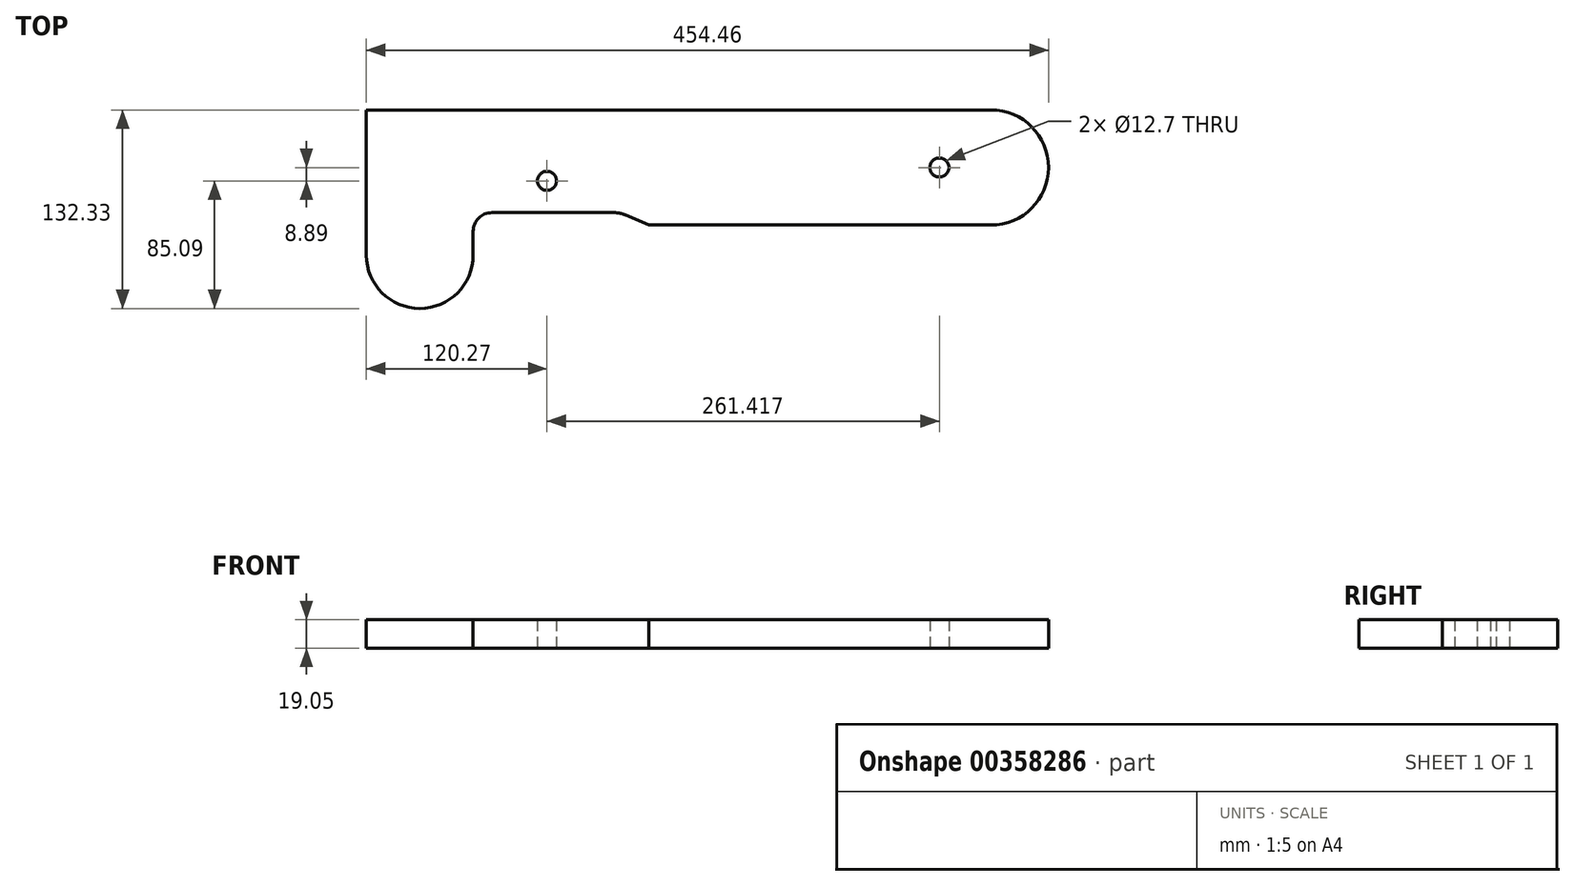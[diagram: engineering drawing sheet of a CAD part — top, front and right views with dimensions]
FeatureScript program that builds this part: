
annotation { "Feature Type Name" : "Feature", "Feature Type Description" : "" }
export const myFeature = defineFeature(function(context is Context, id is Id, definition is map)
    precondition{}
    {
        {
            var Q0;
            Q0=qCreatedBy(makeId("Top.planeOp"),FACE);
            var sketch = newSketch(context, id + "F0", { "sketchPlane" : qUnion([Q0])});
            skCircle(sketch, "E0", {"center": v(0, 0) * mm, "radius": 6.35 * mm});
            skCircle(sketch, "E1", {"center": v(261.42, 8.9) * mm, "radius": 6.35 * mm});
            skArc(sketch, "E2", {"start": v(295.83, -29.46) * mm, "mid": v(334.19, 8.9) * mm, "end": v(295.83, 47.24) * mm});
            skLineSegment(sketch, "E3", {"start": v(295.83, 47.24) * mm, "end": v(-120.27, 47.24) * mm});
            skLineSegment(sketch, "E4", {"start": v(295.83, -29.46) * mm, "end": v(67.82, -29.46) * mm});
            skLineSegment(sketch, "E5", {"start": v(-120.27, 47.24) * mm, "end": v(-120.27, -49.53) * mm});
            skArc(sketch, "E6", {"start": v(-120.27, -49.53) * mm, "mid": v(-84.7, -85.1) * mm, "end": v(-49.15, -49.53) * mm});
            skLineSegment(sketch, "E7", {"start": v(44.87, -21.2) * mm, "end": v(-36.7, -21.2) * mm});
            skLineSegment(sketch, "E8", {"start": v(-49.15, -49.53) * mm, "end": v(-49.15, -33.66) * mm});
            skPoint(sketch, "E9.visualSharp", {"position": v(-49.15, -21.2) * mm});
            skArc(sketch, "E9.filletArc", {"start": v(-36.7, -21.2) * mm, "mid": v(-45.5, -24.85) * mm, "end": v(-49.15, -33.66) * mm});
            skLineSegment(sketch, "E10", {"start": v(52.34, -22.76) * mm, "end": v(67.82, -29.46) * mm});
            skPoint(sketch, "E11.visualSharp", {"position": v(48.77, -21.2) * mm});
            skArc(sketch, "E11.filletArc", {"start": v(52.34, -22.76) * mm, "mid": v(48.69, -21.6) * mm, "end": v(44.87, -21.2) * mm});
            skSolve(sketch);
        }
        {
            var Q0;
            Q0 = qSketchRegion(id + "F0", true);
            extrude(context, id + "F1", {"entities" : qUnion([Q0]), "depth" : 19.05 * mm});
        }
    });
